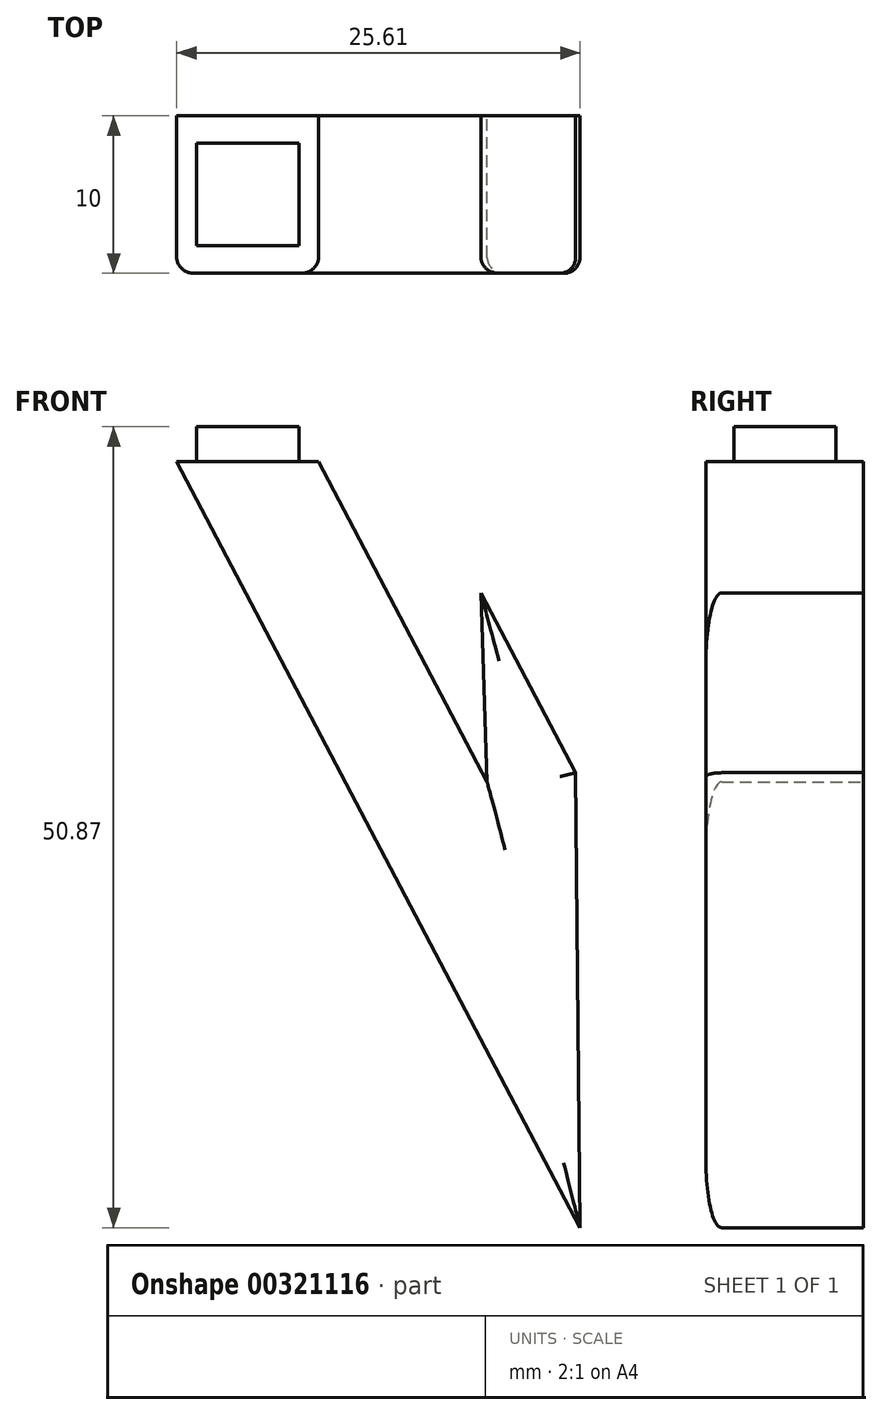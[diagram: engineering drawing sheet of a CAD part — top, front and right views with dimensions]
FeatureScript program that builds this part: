
annotation { "Feature Type Name" : "Feature", "Feature Type Description" : "" }
export const myFeature = defineFeature(function(context is Context, id is Id, definition is map)
    precondition{}
    {
        {
            var Q0;
            Q0=qCreatedBy(makeId("Front.planeOp"),FACE);
            var sketch = newSketch(context, id + "F0", { "sketchPlane" : qUnion([Q0])});
            skLineSegment(sketch, "E0", {"start": v(-25.61, 0) * mm, "end": v(-16.61, 0) * mm});
            skLineSegment(sketch, "E1", {"start": v(-25.61, 0) * mm, "end": v(0, -48.67) * mm});
            skLineSegment(sketch, "E2", {"start": v(0, -48.67) * mm, "end": v(-0.28, -19.77) * mm});
            skLineSegment(sketch, "E3", {"start": v(-0.28, -19.77) * mm, "end": v(-6.29, -8.36) * mm});
            skLineSegment(sketch, "E4", {"start": v(-6.29, -8.36) * mm, "end": v(-5.9, -20.35) * mm});
            skLineSegment(sketch, "E5", {"start": v(-16.61, 0) * mm, "end": v(-5.9, -20.35) * mm});
            skSolve(sketch);
        }
        {
            var Q0;
            Q0 = qSketchRegion(id + "F0", true);
            extrude(context, id + "F1", {"entities" : qUnion([Q0]), "depth" : 10 * mm});
        }
        {
            var Q0;
            Q0=makeQuery(id+"F1.opExtrude","CAP_EDGE",EDGE,{"disambiguationData":[OSD([sQuery(id+"F0.wireOp",EDGE,"E1")])],"isStart":false});
            var Q1;
            Q1=makeQuery(id+"F1.opExtrude","CAP_EDGE",EDGE,{"disambiguationData":[OSD([sQuery(id+"F0.wireOp",EDGE,"E5")])],"isStart":false});
            var Q2;
            Q2=makeQuery(id+"F1.opExtrude","CAP_EDGE",EDGE,{"disambiguationData":[OSD([sQuery(id+"F0.wireOp",EDGE,"E4")])],"isStart":false});
            var Q3;
            Q3=makeQuery(id+"F1.opExtrude","CAP_EDGE",EDGE,{"disambiguationData":[OSD([sQuery(id+"F0.wireOp",EDGE,"E3")])],"isStart":false});
            var Q4;
            Q4=makeQuery(id+"F1.opExtrude","CAP_EDGE",EDGE,{"disambiguationData":[OSD([sQuery(id+"F0.wireOp",EDGE,"E2")])],"isStart":false});
            fillet(context, id + "F2", {"entities" : qUnion([Q0, Q1, Q2, Q3, Q4]), "radius" : 1 * mm, "tangentPropagation" : true, "allowEdgeOverflow" : false});
        }
        {
            var Q0;
            Q0=makeQuery(id+"F1.opExtrude","SWEPT_FACE",FACE,{"disambiguationData":[OSD([sQuery(id+"F0.wireOp",EDGE,"E0")])]});
            var sketch = newSketch(context, id + "F3", { "sketchPlane" : qUnion([Q0])});
            skLineSegment(sketch, "E6.bottom", {"start": v(-24.35, -1.75) * mm, "end": v(-17.86, -1.75) * mm});
            skLineSegment(sketch, "E6.top", {"start": v(-24.35, -8.23) * mm, "end": v(-17.86, -8.23) * mm});
            skLineSegment(sketch, "E6.left", {"start": v(-24.35, -1.75) * mm, "end": v(-24.35, -8.23) * mm});
            skLineSegment(sketch, "E6.right", {"start": v(-17.86, -1.75) * mm, "end": v(-17.86, -8.23) * mm});
            skSolve(sketch);
        }
        {
            var Q0;
            Q0 = qSketchRegion(id + "F3", true);
            extrude(context, id + "F4", {"entities" : qUnion([Q0]), "operationType" : NewBodyOperationType.ADD, "depth" : 2.2 * mm});
        }
    });
